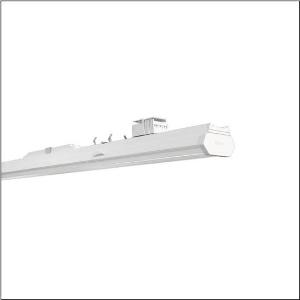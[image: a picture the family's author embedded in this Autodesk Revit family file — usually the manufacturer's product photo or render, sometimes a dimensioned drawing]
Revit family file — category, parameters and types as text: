
# Revit family: licross_11_protected_ho_51td12dn4fxm3c
name_source: partatom
category: Lighting Fixtures
units: mm (PartAtom-declared; Revit-internal decimal feet)

## family parameters
Cut with Voids When Loaded = No
Host = Face
Light Source = No
Part Type = Normal
Room Calculation Point = No
Round Connector Dimension = Use Diameter
Shared = No

## types (1)
- --- (1 x LED, 970 lm, 7.4 W, 4000K)
    Apparent Load = 7 VA
    CIE Flux Codes = 70 91 97 98 100
    Color Rendering = 80
    Color Temperature = 4000K
    Default Elevation = 1800 mm
    Description = Licross 11 Protected HO, luminaire insert, of sheet steel, galvanised, coil coated, white, length: 1.500mm, width: 90mm, height: 101mm, LED rated luminous flux: 15.270lm, light colour: 840, SDCM (Standard Deviation of Colour Matching)MacAdam ≤ 2 SDCM (initial), control gear: DALI 2 (for two DALI lines), with plug, 6-pole, with phase selection, for trunking rail, 14-core, mains connection: 220..240V, AC, 50/60Hz, rated input power: 91W, for trunking rail, 14-core, internal wiring halogen-free, for emergency light function, converter,control gear: single battery element, battery: LiFePO4, 9Ah, primary light control with lens, of plastic, primary optical cover: cover, of PMMA, light emission: direct distribution, primary light characteristic: symmetric, protection rating (complete): IP54, insulation class (complete): insulation class I (protective earthing), certification: CE, UKCA, protection symbol: D if used in an environment with non-conductive dust loads with corresponding accessories, impact resistance: IK06, permissible ambient temperature for indoor applications: +5..+30°C, standard: EN 60598-2-22, LABS conformity tested according to VDMA 24364:2018-05, reducing of maximum allowable ambient temperature of 5°C with ceiling mounting, corresponds to IFS (International Featured Standards) requirements for safety and quality in the food industry, The light source and the operating device comply with the requirements of the Ecodesign Regulation (EU) 2019/2020 and are replaceable in accordance with this regulation, packaging unit: 1 piece
    Height = 92 mm
    Lamp = 1 x LED
    Lamp Light Flux = 970 lm
    Lamp Power = 7.4 W
    Lamp count = 1
    Length = 1500 mm
    Luminous efficacy = 131 lm/W
    Manufacturer = Siteco
    ModVariant = No
    Model = 51TD12DN4FXM3C
    Mounting Place = Ceiling
    Mounting Type = Pendant
    Number of Poles = 1
    OnlyDefault = Yes
    Power Factor = 1
    Product Name = Licross 11 Protected HO
    Product group = luminaire insert | ceiling pendant
    ProductGroupID = 901
    Protection Class = Protection class I
    Protection Degree = IP 54
    RLX_Detail_Level = 1
    RLX_Emergency_Light_Flux = 0 lm
    RLX_Emergency_Type = 0
    RLX_Emergency_Type_DB = No
    RlxData = <blob elided: 25173 chars, md5=90060a84>
    Socket = socket
    Standby Power = 0 W
    System Light Flux = 970 lm
    System Power = 7 W
    Type Comments = : emergency light operation: 3 h
    Type Image = l_1256145.jpg
    URL = http://relux.com
    VarID = @adj_096345
    Voltage = 0 V
    Weight = 0.00 kg
    Width = 88 mm

## geometry (parser evidence)
native form markers: Blend x4, Sweep x11
no freeform markers — native parametric forms only
